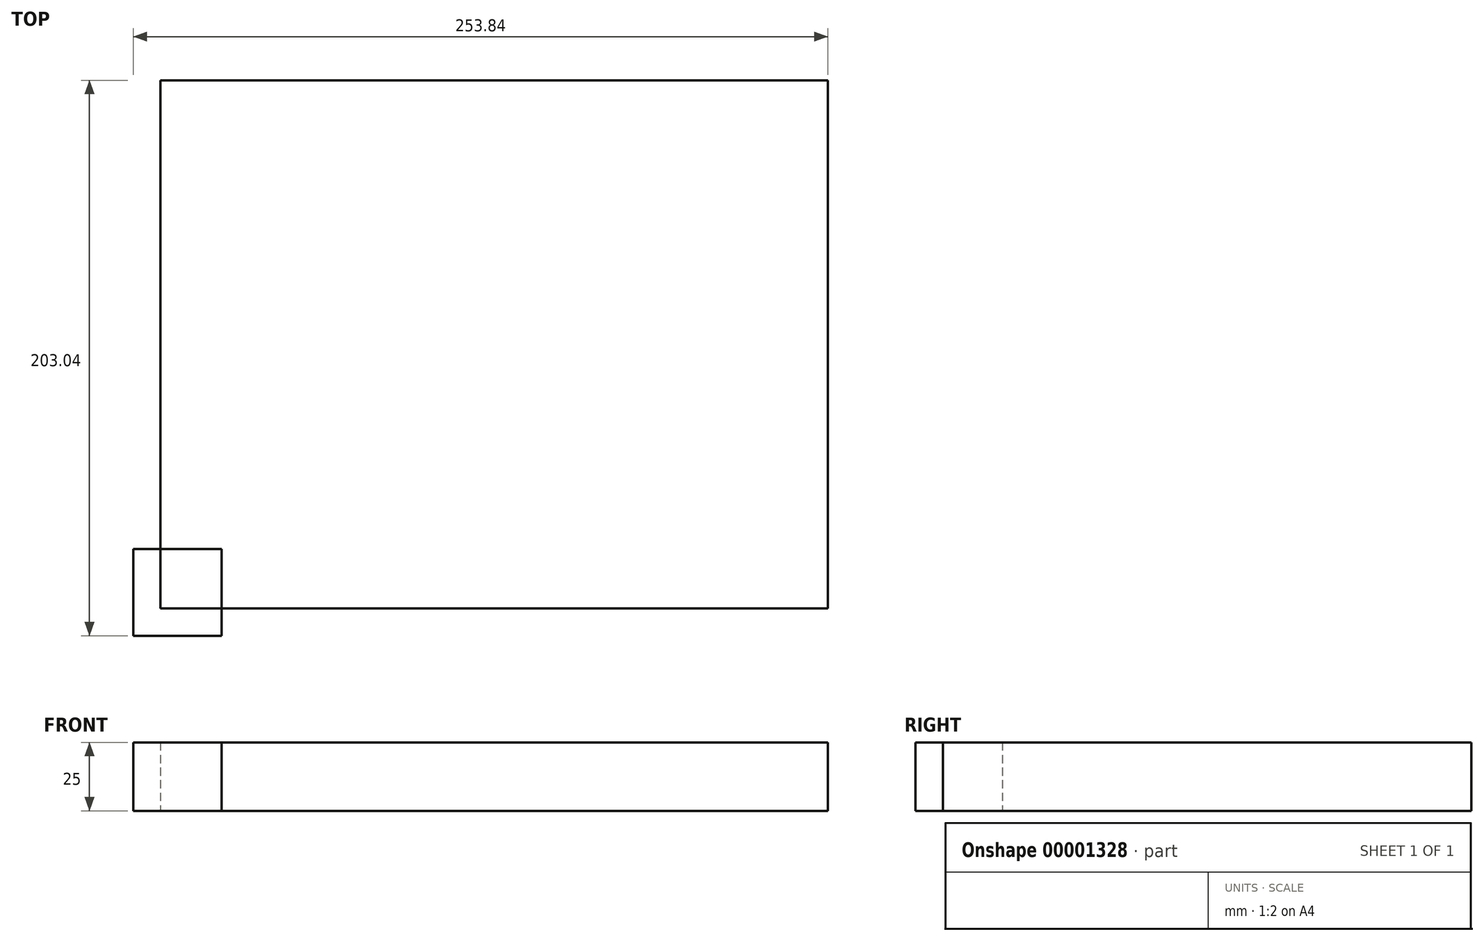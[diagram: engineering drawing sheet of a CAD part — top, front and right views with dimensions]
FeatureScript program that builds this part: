
annotation { "Feature Type Name" : "Feature", "Feature Type Description" : "" }
export const myFeature = defineFeature(function(context is Context, id is Id, definition is map)
    precondition{}
    {
        {
            var Q0;
            Q0=qCreatedBy(makeId("Top.planeOp"),FACE);
            var sketch = newSketch(context, id + "F0", { "sketchPlane" : qUnion([Q0])});
            skLineSegment(sketch, "E0", {"start": v(0, 0) * mm, "end": v(15.24, 0) * mm});
            skLineSegment(sketch, "E1", {"start": v(15.24, 0) * mm, "end": v(15.24, 15.24) * mm});
            skLineSegment(sketch, "E2.bottom", {"start": v(0, 0) * mm, "end": v(243.84, 0) * mm});
            skLineSegment(sketch, "E2.top", {"start": v(0, 193.04) * mm, "end": v(243.84, 193.04) * mm});
            skLineSegment(sketch, "E2.left", {"start": v(0, 0) * mm, "end": v(0, 193.04) * mm});
            skLineSegment(sketch, "E2.right", {"start": v(243.84, 0) * mm, "end": v(243.84, 193.04) * mm});
            skLineSegment(sketch, "E3", {"start": v(0, 0) * mm, "end": v(-10, 0) * mm});
            skLineSegment(sketch, "E4", {"start": v(-10, 0) * mm, "end": v(-10, -10) * mm});
            skLineSegment(sketch, "E5.bottom", {"start": v(-10, -10) * mm, "end": v(22.27, -10) * mm});
            skLineSegment(sketch, "E5.top", {"start": v(-10, 21.7) * mm, "end": v(22.27, 21.7) * mm});
            skLineSegment(sketch, "E5.left", {"start": v(-10, -10) * mm, "end": v(-10, 21.7) * mm});
            skLineSegment(sketch, "E5.right", {"start": v(22.27, -10) * mm, "end": v(22.27, 21.7) * mm});
            skSolve(sketch);
        }
        {
            var Q0;
            {var subQ8=sQuery(id+"F0.wireOp",EDGE,"E2.top");Q0=makeQuery(id+"F0.imprint","IMPRINT",FACE,{"disambiguationData":[TD([[makeQuery(id+"F0.imprint","IMPRINT",EDGE,{"derivedFrom":subQ8}),-1.0]])]});}
            extrude(context, id + "F1", {"entities" : qUnion([Q0]), "depth" : 25 * mm});
        }
        {
            var Q0;
            {var subQ3=sQuery(id+"F0.wireOp",EDGE,"E3");Q0=makeQuery(id+"F0.imprint","IMPRINT",FACE,{"disambiguationData":[TD([[makeQuery(id+"F0.imprint","IMPRINT",EDGE,{"derivedFrom":subQ3}),-1.0]])]});}
            var Q1;
            {var subQ8=sQuery(id+"F0.wireOp",EDGE,"E1");Q1=makeQuery(id+"F0.imprint","IMPRINT",FACE,{"disambiguationData":[TD([[makeQuery(id+"F0.imprint","IMPRINT",EDGE,{"derivedFrom":subQ8}),1.0]])]});}
            var Q2;
            {var subQ5=sQuery(id+"F0.wireOp",EDGE,"E3");Q2=makeQuery(id+"F0.imprint","IMPRINT",FACE,{"disambiguationData":[TD([[makeQuery(id+"F0.imprint","IMPRINT",EDGE,{"derivedFrom":subQ5}),1.0]])]});}
            extrude(context, id + "F2", {"entities" : qUnion([Q0, Q1, Q2]), "depth" : 25 * mm});
        }
    });
